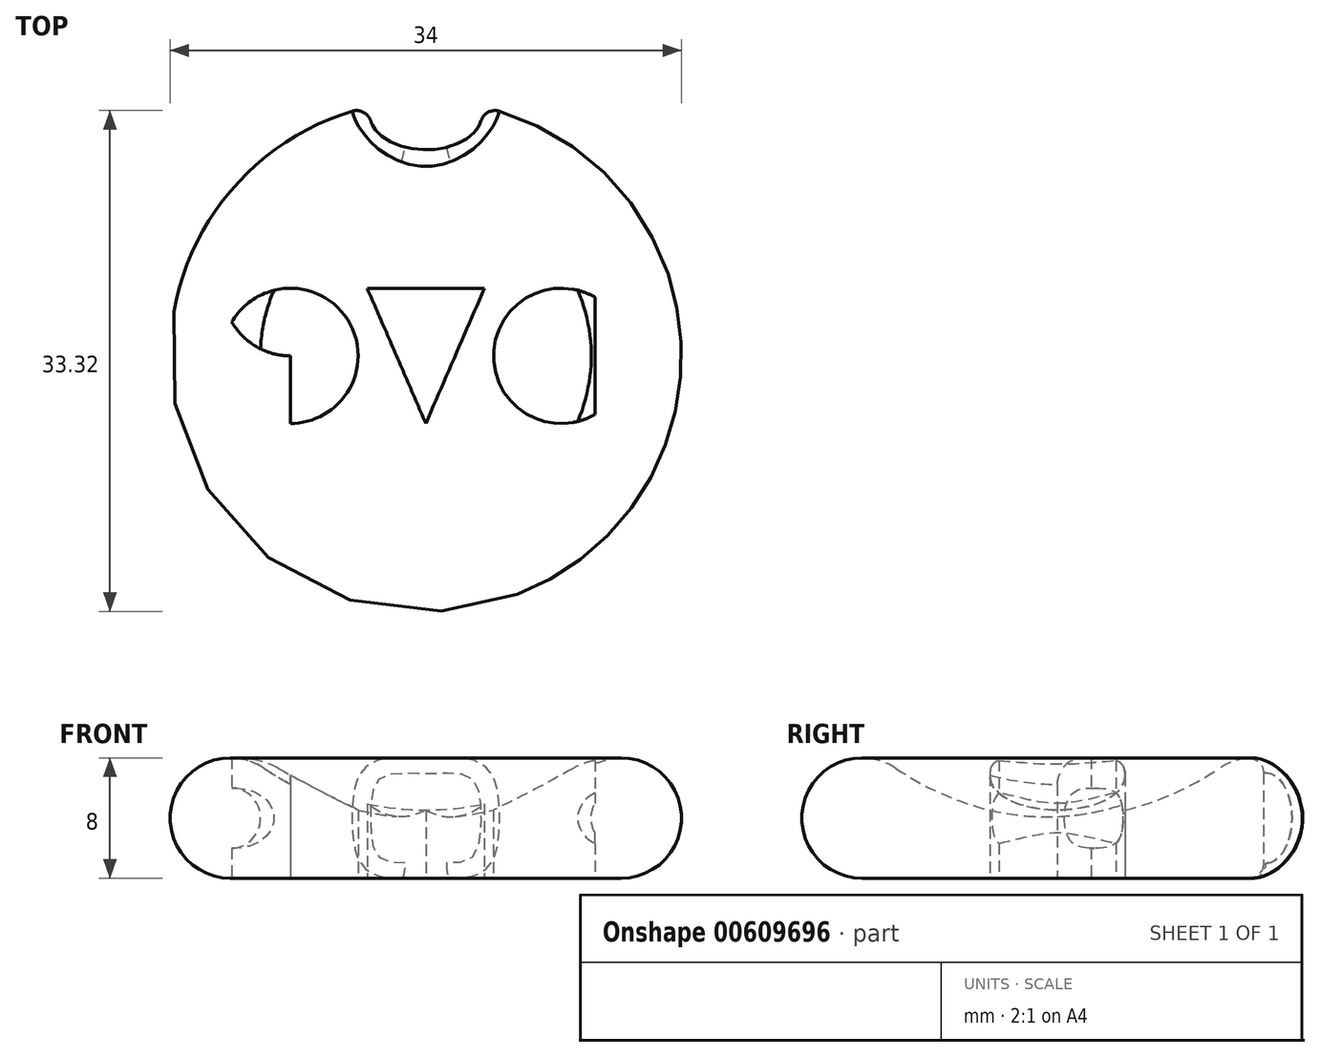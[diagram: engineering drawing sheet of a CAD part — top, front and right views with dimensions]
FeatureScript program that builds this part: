
annotation { "Feature Type Name" : "Feature", "Feature Type Description" : "" }
export const myFeature = defineFeature(function(context is Context, id is Id, definition is map)
    precondition{}
    {
        {
            var Q0;
            Q0=qCreatedBy(makeId("Front.planeOp"),FACE);
            var sketch = newSketch(context, id + "F0", { "sketchPlane" : qUnion([Q0])});
            skArc(sketch, "E0", {"start": v(-10.75, 7.3) * mm, "mid": v(-5.62, 4.85) * mm, "end": v(0, 4) * mm});
            skArc(sketch, "E1", {"start": v(-10.75, 7.3) * mm, "mid": v(-16.82, 5.18) * mm, "end": v(-13, 0) * mm});
            skLineSegment(sketch, "E2", {"start": v(0, 0) * mm, "end": v(-13, 0) * mm});
            skLineSegment(sketch, "E3", {"start": v(-13, 0) * mm, "end": v(0, 0) * mm});
            skLineSegment(sketch, "E4", {"start": v(0, 0) * mm, "end": v(0, 23.13) * mm});
            skLineSegment(sketch, "E5", {"start": v(-17, 0) * mm, "end": v(-17, 29.65) * mm});
            skSolve(sketch);
        }
        {
            var Q0;
            {var subQ0=sQuery(id+"F0.wireOp",EDGE,"E0");Q0=makeQuery(id+"F0.imprint","IMPRINT",FACE,{"disambiguationData":[TD([[makeQuery(id+"F0.imprint","IMPRINT",EDGE,{"derivedFrom":subQ0}),-1.0]])]});}
            var Q1;
            Q1=sQuery(id+"F0.wireOp",EDGE,"E4");
            revolve(context, id + "F1", {"entities" : qUnion([Q0]), "axis" : qUnion([Q1]), "revolveType" : RevolveType.FULL});
        }
        {
            var Q0;
            Q0=qCreatedBy(makeId("Top.planeOp"),FACE);
            var sketch = newSketch(context, id + "F2", { "sketchPlane" : qUnion([Q0])});
            skSolve(sketch);
        }
        {
            var Q0;
            Q0=qCreatedBy(makeId("Front.planeOp"),FACE);
            var sketch = newSketch(context, id + "F3", { "sketchPlane" : qUnion([Q0])});
            skCircle(sketch, "E6", {"center": v(-13, 4) * mm, "radius": 2 * mm});
            skLineSegment(sketch, "E7", {"start": v(0, 0) * mm, "end": v(0, 5.66) * mm});
            skSolve(sketch);
        }
        {
            var Q0;
            Q0=qSketchRegion(id+"F3",true);
            var Q1;
            Q1=sQuery(id+"F3.wireOp",EDGE,"E7");
            revolve(context, id + "F4", {"operationType" : NewBodyOperationType.ADD, "entities" : qUnion([Q0]), "axis" : qUnion([Q1]), "revolveType" : RevolveType.FULL});
        }
        {
            var Q0;
            Q0=qCreatedBy(makeId("Top.planeOp"),FACE);
            var sketch = newSketch(context, id + "F5", { "sketchPlane" : qUnion([Q0])});
            skArc(sketch, "E8", {"start": v(11.25, 3.9) * mm, "mid": v(4.5, 0) * mm, "end": v(11.25, -3.9) * mm});
            skArc(sketch, "E9", {"start": v(-9, -4.5) * mm, "mid": v(-5.1, 2.25) * mm, "end": v(-12.9, 2.25) * mm});
            skLineSegment(sketch, "E10", {"start": v(9, 0) * mm, "end": v(11.25, 0) * mm});
            skLineSegment(sketch, "E11", {"start": v(11.25, -3.9) * mm, "end": v(11.25, 3.9) * mm});
            skLineSegment(sketch, "E12", {"start": v(0, -4.5) * mm, "end": v(0, 4.5) * mm});
            skLineSegment(sketch, "E13", {"start": v(0, 4.5) * mm, "end": v(3.9, 4.5) * mm});
            skLineSegment(sketch, "E14", {"start": v(0, 4.5) * mm, "end": v(-3.9, 4.5) * mm});
            skLineSegment(sketch, "E15", {"start": v(-3.9, 4.5) * mm, "end": v(0, -4.5) * mm});
            skLineSegment(sketch, "E16", {"start": v(3.9, 4.5) * mm, "end": v(0, -4.5) * mm});
            skLineSegment(sketch, "E17", {"start": v(-9, -4.5) * mm, "end": v(-9, 4.5) * mm});
            skArc(sketch, "E18", {"start": v(-12.9, 2.25) * mm, "mid": v(-9, 0) * mm, "end": v(-5.1, 2.25) * mm});
            skPoint(sketch, "E19.center.orphan", {"position": v(0, 0) * mm});
            skSolve(sketch);
        }
        {
            var Q0;
            Q0 = qSketchRegion(id + "F5", true);
            extrude(context, id + "F6", {"entities" : qUnion([Q0]), "operationType" : NewBodyOperationType.REMOVE, "depth" : 37.7 * mm, "offsetDistance" : 25 * mm});
        }
        {
            var Q0;
            Q0 = qSketchRegion(id + "F3", true);
            var Q1;
            Q1=sQuery(id+"F0.wireOp",EDGE,"E4");
            revolve(context, id + "F7", {"operationType" : NewBodyOperationType.ADD, "entities" : qUnion([Q0]), "axis" : qUnion([Q1]), "revolveType" : RevolveType.FULL});
        }
        {
            var Q0;
            Q0=qCreatedBy(makeId("Top.planeOp"),FACE);
            var sketch = newSketch(context, id + "F8", { "sketchPlane" : qUnion([Q0])});
            skLineSegment(sketch, "E20", {"start": v(0, 0) * mm, "end": v(0, 16) * mm});
            skEllipse(sketch, "E21", {"center": v(0, 16) * mm, "majorRadius": 3.7 * mm, "minorRadius": 2.3 * mm, "majorAxis": v(1, 0)});
            skSolve(sketch);
        }
        {
            var Q0;
            Q0=makeQuery(id+"F8.imprint","IMPRINT",FACE,{"disambiguationData":[TD([[makeQuery(id+"F8.imprint","IMPRINT",EDGE,{"derivedFrom":sQuery(id+"F8.wireOp",EDGE,"E21")}),1.0]])]});
            extrude(context, id + "F9", {"entities" : qUnion([Q0]), "operationType" : NewBodyOperationType.REMOVE, "depth" : 40.8 * mm, "offsetDistance" : 25 * mm});
        }
        {
            var Q0;
            Q0=makeQuery(id+"F9.boolean.opBoolean","INTERSECT",EDGE,{"derivedFrom":[makeQuery(id+"F1.opRevolve","SWEPT_FACE",FACE,{"disambiguationData":[OSD([sQuery(id+"F0.wireOp",EDGE,"E1")])]}),makeQuery(id+"F9.opExtrude","SWEPT_FACE",FACE,{"disambiguationData":[OSD([sQuery(id+"F8.wireOp",EDGE,"E21")])]})]});
            fillet(context, id + "F10", {"entities" : qUnion([Q0]), "radius" : (1) * mm, "tangentPropagation" : true, "allowEdgeOverflow" : false});
        }
    });
